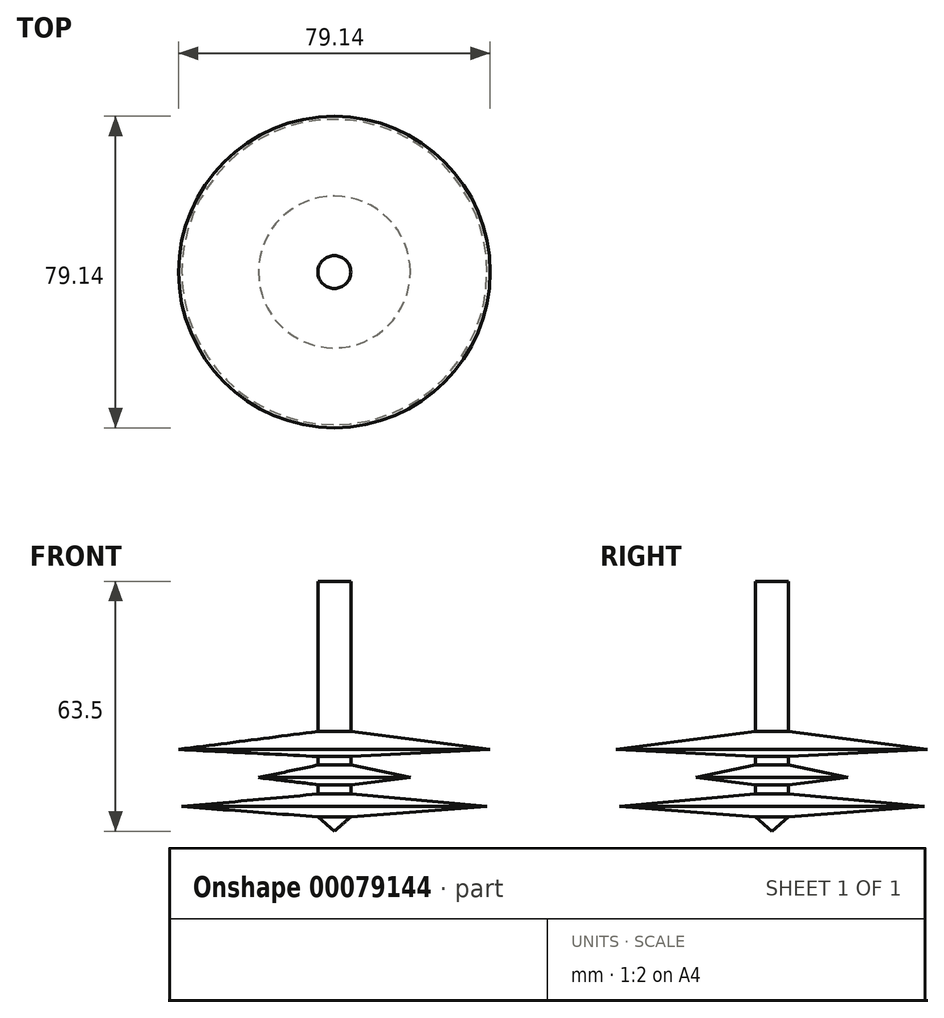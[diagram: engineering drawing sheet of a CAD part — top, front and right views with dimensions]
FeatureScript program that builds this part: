
annotation { "Feature Type Name" : "Feature", "Feature Type Description" : "" }
export const myFeature = defineFeature(function(context is Context, id is Id, definition is map)
    precondition{}
    {
        {
            var Q0;
            Q0=qCreatedBy(makeId("Front.planeOp"),FACE);
            var sketch = newSketch(context, id + "F0", { "sketchPlane" : qUnion([Q0])});
            skLineSegment(sketch, "E0", {"start": v(0, 0) * mm, "end": v(0, 63.5) * mm});
            skLineSegment(sketch, "E1", {"start": v(0, 63.5) * mm, "end": v(4.18, 63.5) * mm});
            skLineSegment(sketch, "E2", {"start": v(4.18, 3.65) * mm, "end": v(0, 0) * mm});
            skLineSegment(sketch, "E3", {"start": v(4.18, 3.65) * mm, "end": v(38.77, 6.26) * mm});
            skLineSegment(sketch, "E4", {"start": v(38.77, 6.26) * mm, "end": v(4.18, 9.44) * mm});
            skLineSegment(sketch, "E5", {"start": v(4.18, 11.83) * mm, "end": v(19.29, 13.62) * mm});
            skLineSegment(sketch, "E6", {"start": v(19.29, 13.62) * mm, "end": v(4.18, 16.8) * mm});
            skLineSegment(sketch, "E7", {"start": v(4.18, 18.99) * mm, "end": v(39.57, 20.78) * mm});
            skLineSegment(sketch, "E8", {"start": v(39.57, 20.78) * mm, "end": v(4.18, 25.35) * mm});
            skLineSegment(sketch, "E9", {"start": v(4.18, 63.5) * mm, "end": v(4.18, 25.35) * mm});
            skLineSegment(sketch, "E10", {"start": v(4.18, 18.99) * mm, "end": v(4.18, 16.8) * mm});
            skLineSegment(sketch, "E11", {"start": v(4.18, 11.83) * mm, "end": v(4.18, 9.44) * mm});
            skSolve(sketch);
        }
        {
            var Q0;
            Q0=makeQuery(id+"F0.imprint","IMPRINT",FACE,{"disambiguationData":[TD([[makeQuery(id+"F0.imprint","IMPRINT",EDGE,{"derivedFrom":sQuery(id+"F0.wireOp",EDGE,"E0")}),-1.0]])]});
            var Q1;
            Q1=sQuery(id+"F0.wireOp",EDGE,"E0");
            revolve(context, id + "F1", {"entities" : qUnion([Q0]), "axis" : qUnion([Q1]), "revolveType" : RevolveType.FULL});
        }
    });
